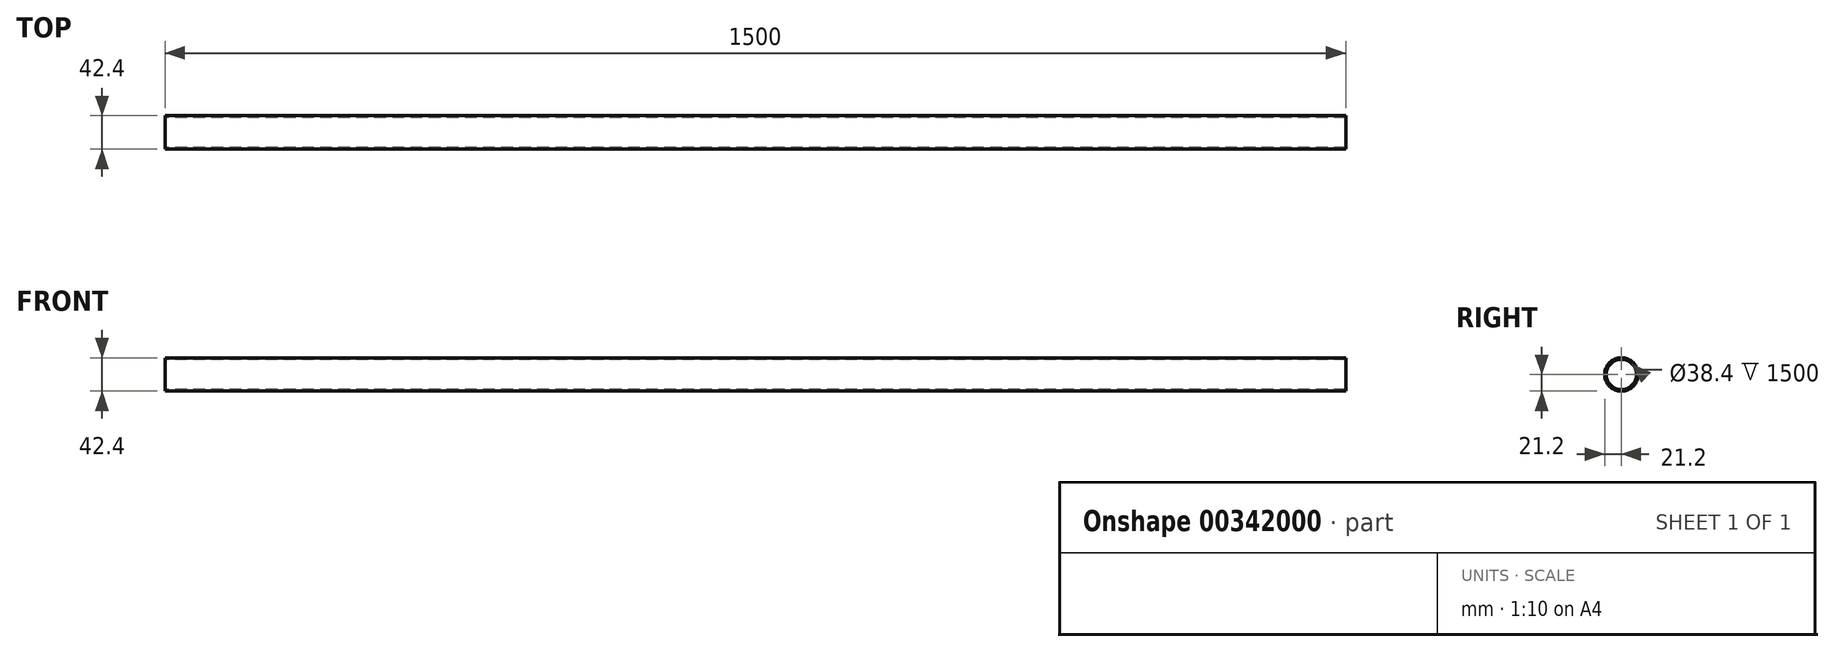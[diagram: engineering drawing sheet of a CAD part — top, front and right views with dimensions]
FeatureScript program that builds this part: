
annotation { "Feature Type Name" : "Feature", "Feature Type Description" : "" }
export const myFeature = defineFeature(function(context is Context, id is Id, definition is map)
    precondition{}
    {
        {
            var Q0;
            Q0=qCreatedBy(makeId("Right.planeOp"),FACE);
            var sketch = newSketch(context, id + "F0", { "sketchPlane" : qUnion([Q0])});
            skCircle(sketch, "E0", {"center": v(0, 0) * mm, "radius": 21.2 * mm});
            skCircle(sketch, "E1", {"center": v(0, 0) * mm, "radius": 19.2 * mm});
            skSolve(sketch);
        }
        {
            var Q0;
            Q0 = qSketchRegion(id + "F0", true);
            extrude(context, id + "F1", {"entities" : qUnion([Q0]), "depth" : 1500 * mm});
        }
    });
